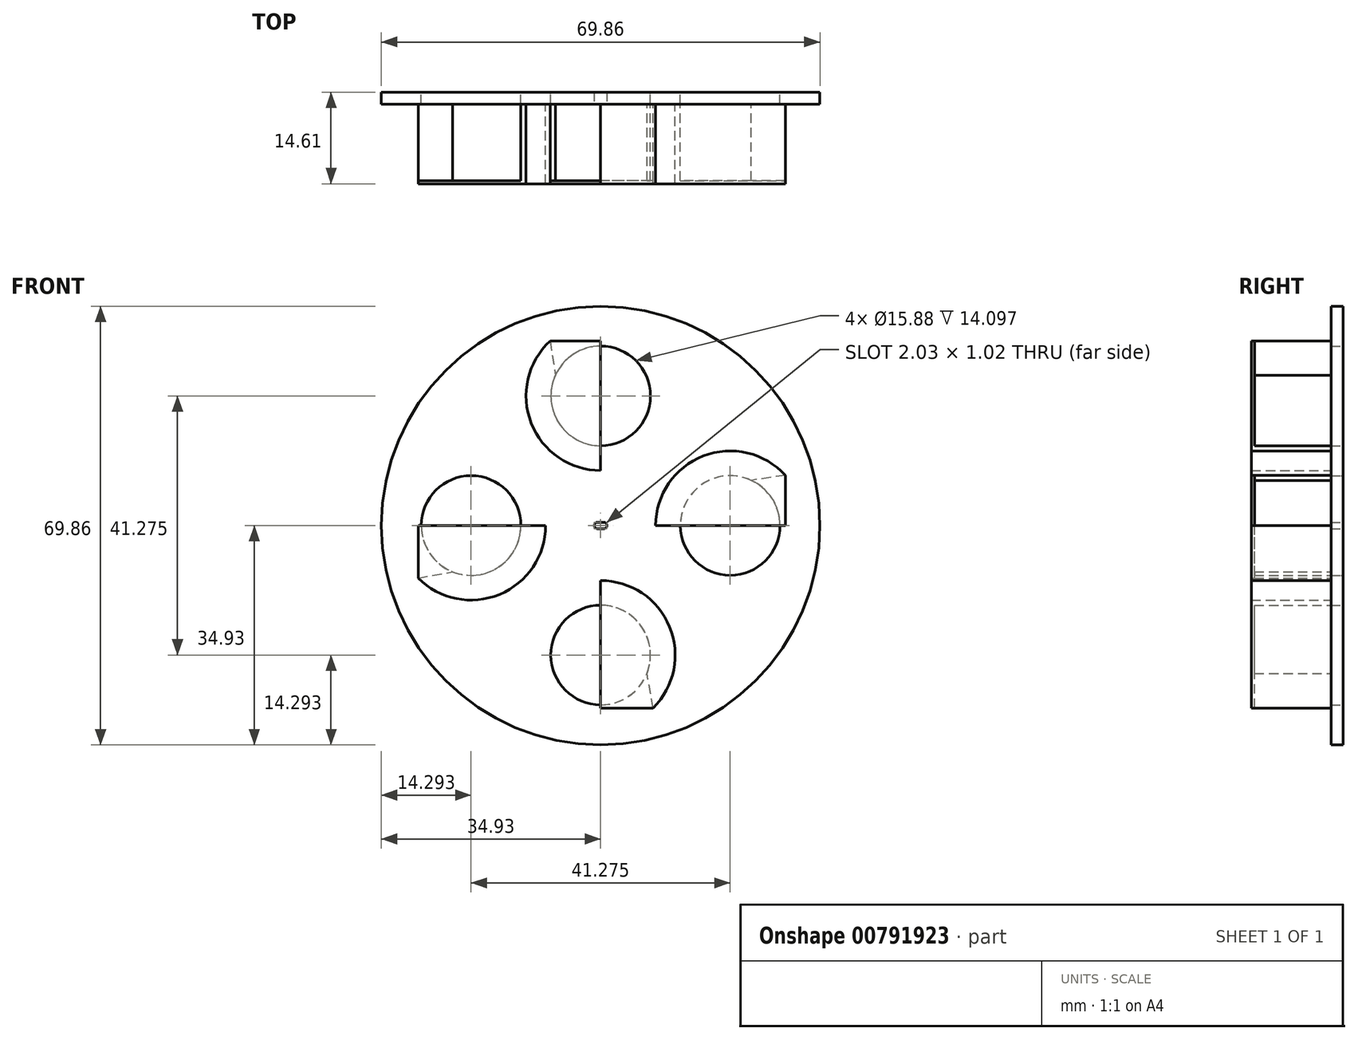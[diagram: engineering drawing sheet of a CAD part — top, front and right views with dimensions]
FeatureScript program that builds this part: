
annotation { "Feature Type Name" : "Feature", "Feature Type Description" : "" }
export const myFeature = defineFeature(function(context is Context, id is Id, definition is map)
    precondition{}
    {
        {
            var Q0;
            Q0=qCreatedBy(makeId("Front.planeOp"),FACE);
            var sketch = newSketch(context, id + "F0", { "sketchPlane" : qUnion([Q0])});
            skCircle(sketch, "E0", {"center": v(0, 0) * mm, "radius": 34.93 * mm});
            skLineSegment(sketch, "E1.bottom", {"start": v(-1.02, 0.5) * mm, "end": v(1.02, 0.5) * mm});
            skLineSegment(sketch, "E1.top", {"start": v(-1.02, -0.5) * mm, "end": v(1.02, -0.5) * mm});
            skLineSegment(sketch, "E1.left", {"start": v(-1.02, 0.5) * mm, "end": v(-1.02, -0.5) * mm});
            skLineSegment(sketch, "E1.right", {"start": v(1.02, 0.5) * mm, "end": v(1.02, -0.5) * mm});
            skLineSegment(sketch, "E2", {"start": v(0, 0) * mm, "end": v(0, 20.64) * mm});
            skLineSegment(sketch, "E3", {"start": v(0, 0) * mm, "end": v(20.64, 0) * mm});
            skLineSegment(sketch, "E4", {"start": v(0, 0) * mm, "end": v(0, -20.64) * mm});
            skLineSegment(sketch, "E5", {"start": v(0, 0) * mm, "end": v(-20.64, 0) * mm});
            skCircle(sketch, "E6", {"center": v(0, 20.64) * mm, "radius": 7.94 * mm});
            skCircle(sketch, "E7", {"center": v(20.64, 0) * mm, "radius": 7.94 * mm});
            skCircle(sketch, "E8", {"center": v(0, -20.64) * mm, "radius": 7.94 * mm});
            skCircle(sketch, "E9", {"center": v(-20.64, 0) * mm, "radius": 7.94 * mm});
            skSolve(sketch);
        }
        {
            var Q0;
            Q0=makeQuery(id+"F0.imprint","IMPRINT",FACE,{"disambiguationData":[TD([[makeQuery(id+"F0.imprint","IMPRINT",EDGE,{"derivedFrom":sQuery(id+"F0.wireOp",EDGE,"E0")}),1.0]])]});
            extrude(context, id + "F1", {"entities" : qUnion([Q0]), "depth" : 1.9 * mm, "offsetDistance" : 25.4 * mm});
        }
        {
            var Q0;
            Q0=makeQuery(id+"F1.opExtrude","CAP_FACE",FACE,{"disambiguationData":[OSD([sQuery(id+"F0.wireOp",EDGE,"E0"),sQuery(id+"F0.wireOp",EDGE,"E1.bottom"),sQuery(id+"F0.wireOp",EDGE,"E1.top"),sQuery(id+"F0.wireOp",EDGE,"E1.left"),sQuery(id+"F0.wireOp",EDGE,"E1.right"),sQuery(id+"F0.wireOp",EDGE,"E6"),sQuery(id+"F0.wireOp",EDGE,"E7"),sQuery(id+"F0.wireOp",EDGE,"E8"),sQuery(id+"F0.wireOp",EDGE,"E9")])],"isStart":false});
            var sketch = newSketch(context, id + "F2", { "sketchPlane" : qUnion([Q0])});
            skLineSegment(sketch, "E10", {"start": v(0, 0) * mm, "end": v(0, 8.76) * mm, "construction": true});
            skLineSegment(sketch, "E11", {"start": v(0, 0) * mm, "end": v(8.76, 0) * mm, "construction": true});
            skLineSegment(sketch, "E12", {"start": v(0, 0) * mm, "end": v(0, -8.76) * mm, "construction": true});
            skLineSegment(sketch, "E13", {"start": v(0, 0) * mm, "end": v(-8.76, 0) * mm, "construction": true});
            skPoint(sketch, "E13.endSnap0", {"position": v(-1.02, 0) * mm});
            skPoint(sketch, "E14", {"position": v(-20.64, 0) * mm});
            skPoint(sketch, "E15", {"position": v(20.64, 0) * mm});
            skPoint(sketch, "E16", {"position": v(0, 20.64) * mm});
            skPoint(sketch, "E17", {"position": v(0, -20.64) * mm});
            skArc(sketch, "E18", {"start": v(-8.05, 29.37) * mm, "mid": v(-11.06, 16.32) * mm, "end": v(0, 8.76) * mm});
            skArc(sketch, "E19", {"start": v(29.4, 8) * mm, "mid": v(16.34, 11.07) * mm, "end": v(8.76, 0) * mm});
            skArc(sketch, "E20", {"start": v(-29.06, -8.37) * mm, "mid": v(-16.11, -10.98) * mm, "end": v(-8.76, 0) * mm});
            skArc(sketch, "E21", {"start": v(8.36, -29.07) * mm, "mid": v(10.98, -16.12) * mm, "end": v(0, -8.76) * mm});
            skPoint(sketch, "E22", {"position": v(-8.05, 29.37) * mm});
            skPoint(sketch, "E23", {"position": v(29.4, 8) * mm});
            skPoint(sketch, "E24", {"position": v(8.36, -29.07) * mm});
            skPoint(sketch, "E25", {"position": v(-29.06, -8.37) * mm});
            skLineSegment(sketch, "E26", {"start": v(-8.05, 29.37) * mm, "end": v(-5.9, 15.32) * mm});
            skLineSegment(sketch, "E27", {"start": v(29.4, 8) * mm, "end": v(15.32, 5.9) * mm});
            skLineSegment(sketch, "E28", {"start": v(8.36, -29.07) * mm, "end": v(5.89, -15.32) * mm});
            skLineSegment(sketch, "E29", {"start": v(-29.06, -8.37) * mm, "end": v(-15.31, -5.89) * mm});
            skLineSegment(sketch, "E30", {"start": v(-8.76, 0) * mm, "end": v(-12.7, 0) * mm});
            skLineSegment(sketch, "E31", {"start": v(8.76, 0) * mm, "end": v(12.7, 0) * mm});
            skLineSegment(sketch, "E32", {"start": v(0, -8.76) * mm, "end": v(0, -12.7) * mm});
            skLineSegment(sketch, "E33", {"start": v(0, 8.76) * mm, "end": v(0, 12.7) * mm});
            skSolve(sketch);
        }
        {
            var Q0;
            Q0=makeQuery(id+"F2.imprint","IMPRINT",FACE,{"disambiguationData":[TD([[makeQuery(id+"F2.imprint","IMPRINT",EDGE,{"derivedFrom":sQuery(id+"F2.wireOp",EDGE,"E18")}),1.0]])]});
            var Q1;
            Q1=makeQuery(id+"F2.imprint","IMPRINT",FACE,{"disambiguationData":[TD([[makeQuery(id+"F2.imprint","IMPRINT",EDGE,{"derivedFrom":sQuery(id+"F2.wireOp",EDGE,"E20")}),1.0]])]});
            var Q2;
            Q2=makeQuery(id+"F2.imprint","IMPRINT",FACE,{"disambiguationData":[TD([[makeQuery(id+"F2.imprint","IMPRINT",EDGE,{"derivedFrom":sQuery(id+"F2.wireOp",EDGE,"E19")}),1.0]])]});
            var Q3;
            Q3=makeQuery(id+"F2.imprint","IMPRINT",FACE,{"disambiguationData":[TD([[makeQuery(id+"F2.imprint","IMPRINT",EDGE,{"derivedFrom":sQuery(id+"F2.wireOp",EDGE,"E21")}),1.0]])]});
            extrude(context, id + "F3", {"entities" : qUnion([Q0, Q1, Q2, Q3]), "operationType" : NewBodyOperationType.ADD, "depth" : 12.7 * mm, "offsetDistance" : 25.4 * mm});
        }
        {
            var Q0;
            Q0=makeQuery(id+"F3.opExtrude","CAP_FACE",FACE,{"disambiguationData":[OSD([sQuery(id+"F0.wireOp",EDGE,"E9"),sQuery(id+"F2.wireOp",EDGE,"E20"),sQuery(id+"F2.wireOp",EDGE,"E29"),sQuery(id+"F2.wireOp",EDGE,"E30")])],"isStart":false});
            var sketch = newSketch(context, id + "F4", { "sketchPlane" : qUnion([Q0])});
            skLineSegment(sketch, "E34", {"start": v(-20.64, 0) * mm, "end": v(-12.7, 0) * mm});
            skLineSegment(sketch, "E35", {"start": v(-23.57, -7.38) * mm, "end": v(-23.57, 0) * mm});
            skLineSegment(sketch, "E36", {"start": v(-23.57, 0) * mm, "end": v(-20.64, 0) * mm});
            skLineSegment(sketch, "E37", {"start": v(-29.06, -8.37) * mm, "end": v(-29.06, 0) * mm});
            skLineSegment(sketch, "E38", {"start": v(-29.06, 0) * mm, "end": v(-23.57, 0) * mm});
            skSolve(sketch);
        }
        {
            var Q0;
            Q0=makeQuery(id+"F3.opExtrude","CAP_FACE",FACE,{"disambiguationData":[OSD([sQuery(id+"F0.wireOp",EDGE,"E8"),sQuery(id+"F2.wireOp",EDGE,"E21"),sQuery(id+"F2.wireOp",EDGE,"E28"),sQuery(id+"F2.wireOp",EDGE,"E32")])],"isStart":false});
            var sketch = newSketch(context, id + "F5", { "sketchPlane" : qUnion([Q0])});
            skLineSegment(sketch, "E39", {"start": v(0, -20.64) * mm, "end": v(0, -12.7) * mm});
            skLineSegment(sketch, "E40", {"start": v(7.37, -23.57) * mm, "end": v(0, -23.57) * mm});
            skLineSegment(sketch, "E41", {"start": v(0, -23.57) * mm, "end": v(0, -20.64) * mm});
            skLineSegment(sketch, "E42", {"start": v(8.36, -29.07) * mm, "end": v(0, -29.07) * mm});
            skLineSegment(sketch, "E43", {"start": v(0, -29.07) * mm, "end": v(0, -23.57) * mm});
            skSolve(sketch);
        }
        {
            var Q0;
            Q0=makeQuery(id+"F3.opExtrude","CAP_FACE",FACE,{"disambiguationData":[OSD([sQuery(id+"F0.wireOp",EDGE,"E7"),sQuery(id+"F2.wireOp",EDGE,"E19"),sQuery(id+"F2.wireOp",EDGE,"E27"),sQuery(id+"F2.wireOp",EDGE,"E31")])],"isStart":false});
            var sketch = newSketch(context, id + "F6", { "sketchPlane" : qUnion([Q0])});
            skLineSegment(sketch, "E44", {"start": v(12.7, 0) * mm, "end": v(20.64, 0) * mm});
            skLineSegment(sketch, "E45", {"start": v(20.64, 0) * mm, "end": v(24, 0) * mm});
            skLineSegment(sketch, "E46", {"start": v(24, 0) * mm, "end": v(24, 7.2) * mm});
            skLineSegment(sketch, "E47", {"start": v(29.4, 8) * mm, "end": v(29.4, 0) * mm});
            skLineSegment(sketch, "E48", {"start": v(29.4, 0) * mm, "end": v(24, 0) * mm});
            skSolve(sketch);
        }
        {
            var Q0;
            Q0=makeQuery(id+"F3.opExtrude","CAP_FACE",FACE,{"disambiguationData":[OSD([sQuery(id+"F0.wireOp",EDGE,"E6"),sQuery(id+"F2.wireOp",EDGE,"E18"),sQuery(id+"F2.wireOp",EDGE,"E26"),sQuery(id+"F2.wireOp",EDGE,"E33")])],"isStart":false});
            var sketch = newSketch(context, id + "F7", { "sketchPlane" : qUnion([Q0])});
            skLineSegment(sketch, "E49", {"start": v(-7.22, 23.94) * mm, "end": v(0, 23.94) * mm});
            skLineSegment(sketch, "E50", {"start": v(0, 23.94) * mm, "end": v(0, 20.64) * mm});
            skLineSegment(sketch, "E51", {"start": v(0, 20.64) * mm, "end": v(0, 12.7) * mm});
            skLineSegment(sketch, "E52", {"start": v(-8.05, 29.37) * mm, "end": v(0, 29.37) * mm});
            skLineSegment(sketch, "E53", {"start": v(0, 29.37) * mm, "end": v(0, 23.94) * mm});
            skSolve(sketch);
        }
        {
            var Q0;
            Q0=makeQuery(id+"F4.imprint","IMPRINT",FACE,{"disambiguationData":[TD([[makeQuery(id+"F4.imprint","IMPRINT",EDGE,{"derivedFrom":sQuery(id+"F4.wireOp",EDGE,"E34")}),-1.0]])]});
            var Q1;
            Q1=makeQuery(id+"F7.imprint","IMPRINT",FACE,{"disambiguationData":[TD([[makeQuery(id+"F7.imprint","IMPRINT",EDGE,{"derivedFrom":sQuery(id+"F7.wireOp",EDGE,"E49")}),-1.0]])]});
            var Q2;
            Q2=makeQuery(id+"F6.imprint","IMPRINT",FACE,{"disambiguationData":[TD([[makeQuery(id+"F6.imprint","IMPRINT",EDGE,{"derivedFrom":sQuery(id+"F6.wireOp",EDGE,"E44")}),1.0]])]});
            var Q3;
            Q3=makeQuery(id+"F5.imprint","IMPRINT",FACE,{"disambiguationData":[TD([[makeQuery(id+"F5.imprint","IMPRINT",EDGE,{"derivedFrom":sQuery(id+"F5.wireOp",EDGE,"E39")}),-1.0]])]});
            var Q4;
            Q4=makeQuery(id+"F4.imprint","IMPRINT",FACE,{"disambiguationData":[TD([[makeQuery(id+"F4.imprint","IMPRINT",EDGE,{"derivedFrom":sQuery(id+"F4.wireOp",EDGE,"E35")}),1.0]])]});
            var Q5;
            Q5=makeQuery(id+"F7.imprint","IMPRINT",FACE,{"disambiguationData":[TD([[makeQuery(id+"F7.imprint","IMPRINT",EDGE,{"derivedFrom":sQuery(id+"F7.wireOp",EDGE,"E49")}),1.0]])]});
            var Q6;
            Q6=makeQuery(id+"F6.imprint","IMPRINT",FACE,{"disambiguationData":[TD([[makeQuery(id+"F6.imprint","IMPRINT",EDGE,{"derivedFrom":sQuery(id+"F6.wireOp",EDGE,"E46")}),-1.0]])]});
            var Q7;
            Q7=makeQuery(id+"F5.imprint","IMPRINT",FACE,{"disambiguationData":[TD([[makeQuery(id+"F5.imprint","IMPRINT",EDGE,{"derivedFrom":sQuery(id+"F5.wireOp",EDGE,"E40")}),1.0]])]});
            extrude(context, id + "F8", {"entities" : qUnion([Q0, Q1, Q2, Q3, Q4, Q5, Q6, Q7]), "operationType" : NewBodyOperationType.ADD, "oppositeDirection" : true, "depth" : 0.5 * mm, "offsetDistance" : 25.4 * mm});
        }
        {
            var Q0;
            Q0=makeQuery(id+"F1.opExtrude","SWEPT_EDGE",EDGE,{"disambiguationData":[OSD([sQuery(id+"F0.wireOp",EDGE,"E1.bottom"),sQuery(id+"F0.wireOp",EDGE,"E1.right")])]});
            var Q1;
            Q1=makeQuery(id+"F1.opExtrude","SWEPT_EDGE",EDGE,{"disambiguationData":[OSD([sQuery(id+"F0.wireOp",EDGE,"E1.top"),sQuery(id+"F0.wireOp",EDGE,"E1.right")])]});
            var Q2;
            Q2=makeQuery(id+"F1.opExtrude","SWEPT_EDGE",EDGE,{"disambiguationData":[OSD([sQuery(id+"F0.wireOp",EDGE,"E1.top"),sQuery(id+"F0.wireOp",EDGE,"E1.left")])]});
            var Q3;
            Q3=makeQuery(id+"F1.opExtrude","SWEPT_EDGE",EDGE,{"disambiguationData":[OSD([sQuery(id+"F0.wireOp",EDGE,"E1.bottom"),sQuery(id+"F0.wireOp",EDGE,"E1.left")])]});
            fillet(context, id + "F9", {"entities" : qUnion([Q0, Q1, Q2, Q3]), "radius" : 0.5 * mm, "tangentPropagation" : true, "allowEdgeOverflow" : false});
        }
    });
